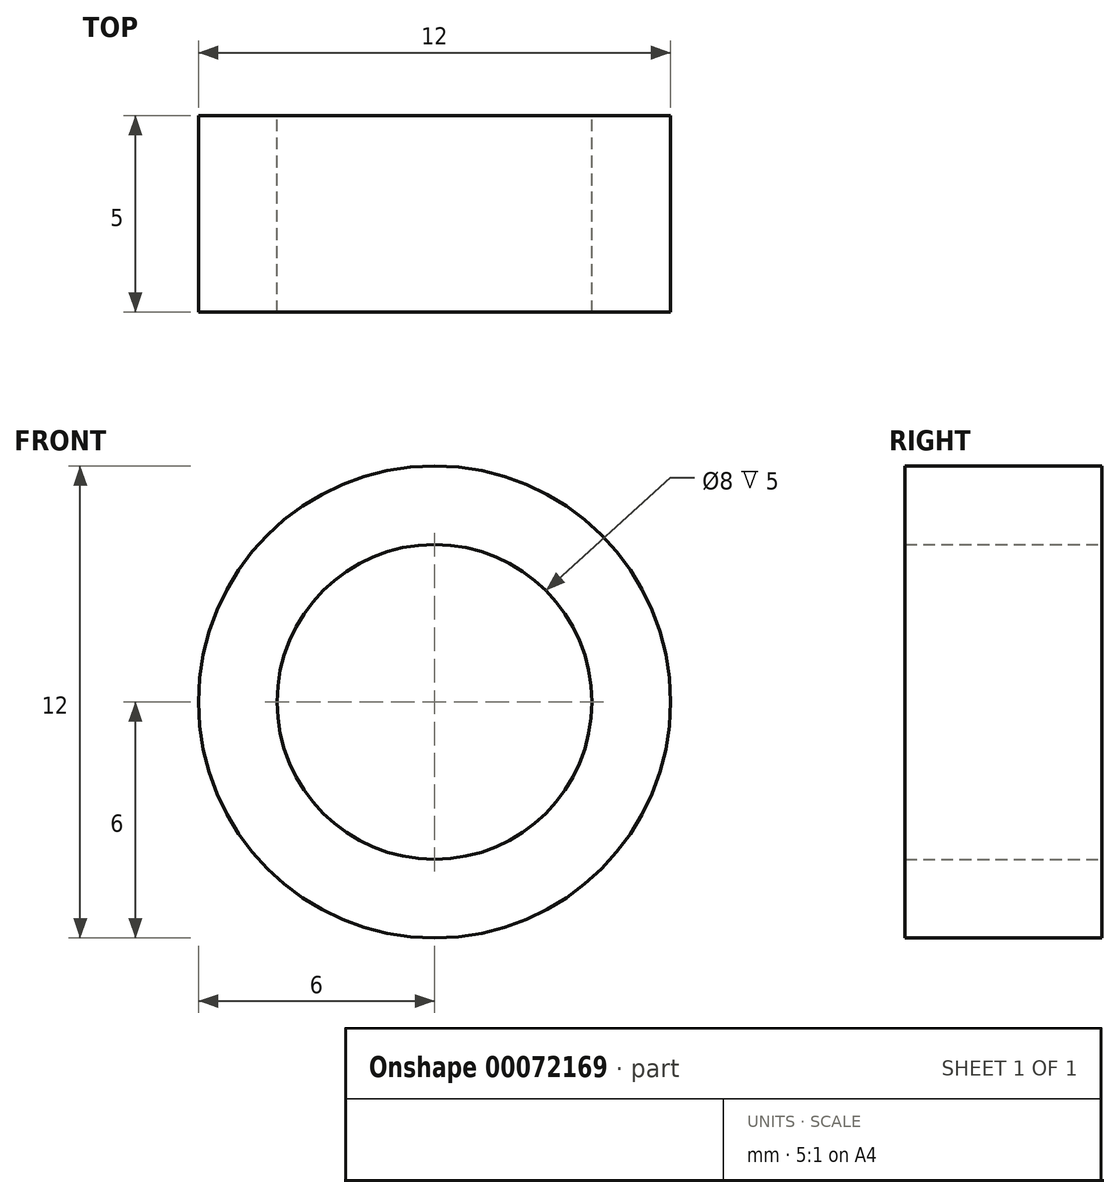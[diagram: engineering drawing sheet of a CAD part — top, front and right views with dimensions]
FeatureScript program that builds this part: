
annotation { "Feature Type Name" : "Feature", "Feature Type Description" : "" }
export const myFeature = defineFeature(function(context is Context, id is Id, definition is map)
    precondition{}
    {
        {
            var Q0;
            Q0=qCreatedBy(makeId("Front.planeOp"),FACE);
            var sketch = newSketch(context, id + "F0", { "sketchPlane" : qUnion([Q0])});
            skCircle(sketch, "E0", {"center": v(0, 0) * mm, "radius": 4 * mm});
            skCircle(sketch, "E1.0", {"center": v(0, 0) * mm, "radius": 6 * mm});
            skSolve(sketch);
        }
        {
            var Q0;
            Q0 = qSketchRegion(id + "F0", true);
            extrude(context, id + "F1", {"entities" : qUnion([Q0]), "depth" : 5 * mm});
        }
    });
